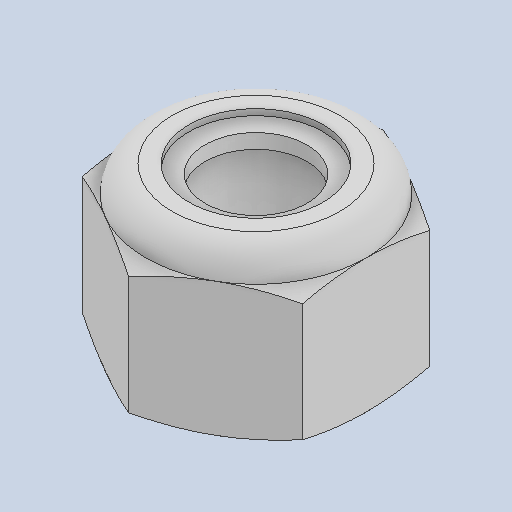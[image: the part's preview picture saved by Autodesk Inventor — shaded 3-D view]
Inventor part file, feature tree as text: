
AUTODESK INVENTOR PART (.ipt)
format: ipt  version: 2024.2 (Build 282272000, 272)  size: 172,032 bytes
history: native  units: in
note: dims shown in document units (in); Inventor stores cm internally (conversion verified against a paired STEP export)
features: other x1, revolve x1
ambient origin geometry x8: Origin, YZ Plane, XZ Plane, XY Plane, X Axis, Y Axis, Z Axis, Center Point
bodies: Solid1 (feature_tree), Solid2 (feature_tree)
feature tree (2):
  other  "Cut-Revolve4"
  revolve  "Revolve2"  [1 undecoded]
note: 1 required parameter value undecoded (feature->parameter linkage not recoverable at this tier; creation-order binding heuristic only, values carry confidence <= 0.55)
